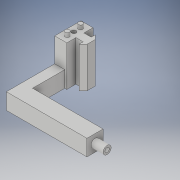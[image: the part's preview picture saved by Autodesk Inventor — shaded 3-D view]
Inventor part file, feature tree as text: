
AUTODESK INVENTOR PART (.ipt)
format: ipt  version: 2018 (Build 220112000, 112)  size: 165,376 bytes
history: native  units: in
note: dims shown in document units (in); Inventor stores cm internally (conversion verified against a paired STEP export)
features: sketch x7, extrude x5, hole x2
ambient origin geometry x8: Origin, YZ Plane, XZ Plane, XY Plane, X Axis, Y Axis, Z Axis, Center Point
bodies: Solid1 (feature_tree)
feature tree (14):
  extrude  "Extrusion1"  Depth=0.65in
  extrude  "Extrusion2"  Depth=0.28in
  hole  "Hole1"  [1 undecoded]
  extrude  "Extrusion6"  Depth=0.1in
  extrude  "Extrusion7"  Depth=1.0in
  extrude  "Extrusion8"  Depth=0.11in
  hole  "Hole3"  [1 undecoded]
  sketch  "Sketch1"  dims[d0=0.3in d1=0.65in]
  sketch  "Sketch2"  dims[d2=0.225in d3=0.28in]
  sketch  "Sketch3"  dims[d4=0.2in d5=0.1in]
  sketch  "Sketch8"  dims[d6=0.1in d7=0.1in]
  sketch  "Sketch9"  dims[d8=1.0in d9=0.0in d10=0.16in]
  sketch  "Sketch10"  dims[d11=0.16in d12=0.11in]
  sketch  "Sketch11"  dims[d13=0.11in d14=0.1in d15=0.0in d16=0.325in d17=0.11in d18=0.75in d19=0.375in d20=0.25in d21=0.5635in d22=0.45in d23=0.8108in d43=0.25in d44=0.4in d45=1.2in d46=0.0in d47=0.4in d48=1.75in d49=0.0in d50=0.2in d51=0.2in d52=0.3in d53=0.0in d54=0.11in d55=0.11in d56=0.75in d57=0.375in d58=0.25in d59=0.5635in d60=0.63in d61=0.8108in]
note: 2 required parameter values undecoded (feature->parameter linkage not recoverable at this tier; creation-order binding heuristic only, values carry confidence <= 0.55)
